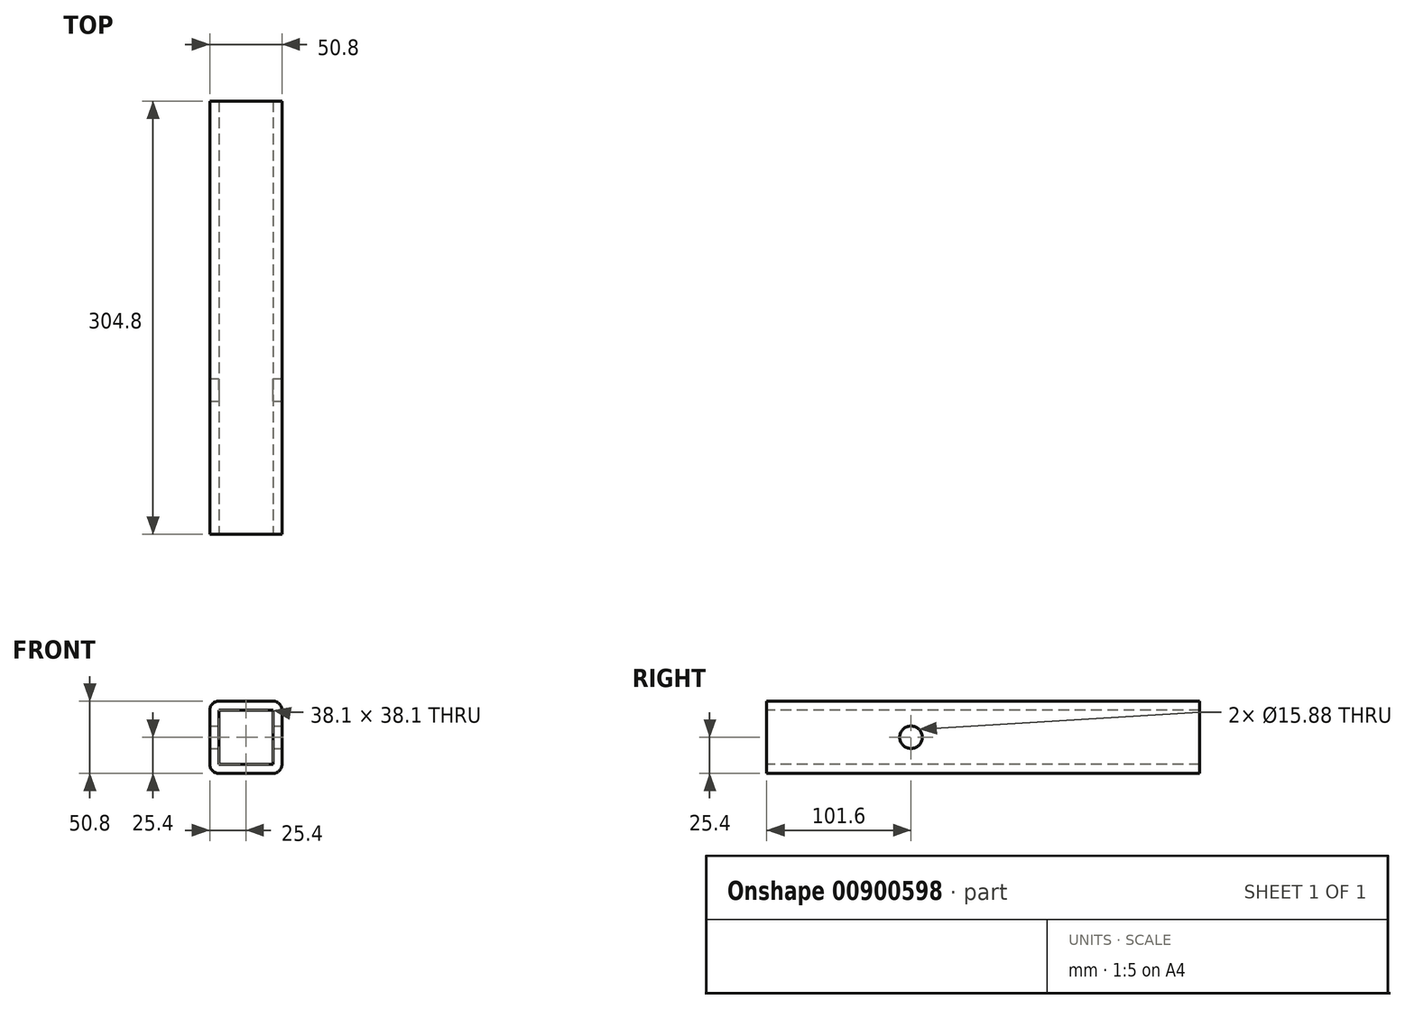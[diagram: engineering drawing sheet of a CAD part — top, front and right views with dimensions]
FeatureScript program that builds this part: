
annotation { "Feature Type Name" : "Feature", "Feature Type Description" : "" }
export const myFeature = defineFeature(function(context is Context, id is Id, definition is map)
    precondition{}
    {
        {
            var Q0;
            Q0=qCreatedBy(makeId("Front.planeOp"),FACE);
            var sketch = newSketch(context, id + "F0", { "sketchPlane" : qUnion([Q0])});
            skLineSegment(sketch, "E0", {"start": v(-6.35, 0) * mm, "end": v(-44.45, 0) * mm});
            skLineSegment(sketch, "E1", {"start": v(-50.8, 6.35) * mm, "end": v(-50.8, 44.45) * mm});
            skLineSegment(sketch, "E2", {"start": v(-44.45, 50.8) * mm, "end": v(-6.35, 50.8) * mm});
            skLineSegment(sketch, "E3", {"start": v(0, 44.45) * mm, "end": v(0, 6.35) * mm});
            skPoint(sketch, "E4.visualSharp", {"position": v(-50.8, 50.8) * mm});
            skArc(sketch, "E4.filletArc", {"start": v(-44.45, 50.8) * mm, "mid": v(-48.94, 48.94) * mm, "end": v(-50.8, 44.45) * mm});
            skPoint(sketch, "E5.visualSharp", {"position": v(0, 50.8) * mm});
            skArc(sketch, "E5.filletArc", {"start": v(0, 44.45) * mm, "mid": v(-1.86, 48.94) * mm, "end": v(-6.35, 50.8) * mm});
            skPoint(sketch, "E6.visualSharp", {"position": v(0, 0) * mm});
            skArc(sketch, "E6.filletArc", {"start": v(-6.35, 0) * mm, "mid": v(-1.86, 1.86) * mm, "end": v(0, 6.35) * mm});
            skPoint(sketch, "E7.visualSharp", {"position": v(-50.8, 0) * mm});
            skArc(sketch, "E7.filletArc", {"start": v(-50.8, 6.35) * mm, "mid": v(-48.94, 1.86) * mm, "end": v(-44.45, 0) * mm});
            skSolve(sketch);
        }
        {
            var Q0;
            Q0 = qSketchRegion(id + "F0", true);
            extrude(context, id + "F1", {"entities" : qUnion([Q0]), "depth" : 304.8 * mm, "offsetDistance" : 25.4 * mm});
        }
        {
            var Q0;
            Q0=makeQuery(id+"F1.opExtrude","CAP_FACE",FACE,{"disambiguationData":[OSD([sQuery(id+"F0.wireOp",EDGE,"E0"),sQuery(id+"F0.wireOp",EDGE,"E1"),sQuery(id+"F0.wireOp",EDGE,"E2"),sQuery(id+"F0.wireOp",EDGE,"E3"),sQuery(id+"F0.wireOp",EDGE,"E4.filletArc"),sQuery(id+"F0.wireOp",EDGE,"E5.filletArc"),sQuery(id+"F0.wireOp",EDGE,"E6.filletArc"),sQuery(id+"F0.wireOp",EDGE,"E7.filletArc")])],"isStart":false});
            var sketch = newSketch(context, id + "F2", { "sketchPlane" : qUnion([Q0])});
            skLineSegment(sketch, "E8", {"start": v(-44.45, 6.35) * mm, "end": v(-6.35, 6.35) * mm});
            skLineSegment(sketch, "E9", {"start": v(-6.35, 6.35) * mm, "end": v(-6.35, 44.45) * mm});
            skLineSegment(sketch, "E10", {"start": v(-6.35, 44.45) * mm, "end": v(-44.45, 44.45) * mm});
            skLineSegment(sketch, "E11", {"start": v(-44.45, 44.45) * mm, "end": v(-44.45, 6.35) * mm});
            skSolve(sketch);
        }
        {
            var Q0;
            Q0 = qSketchRegion(id + "F2", true);
            extrude(context, id + "F3", {"entities" : qUnion([Q0]), "operationType" : NewBodyOperationType.REMOVE, "oppositeDirection" : true, "depth" : 304.8 * mm, "offsetDistance" : 25.4 * mm});
        }
        {
            var Q0;
            Q0=makeQuery(id+"F1.opExtrude","SWEPT_FACE",FACE,{"disambiguationData":[OSD([sQuery(id+"F0.wireOp",EDGE,"E3")])]});
            var sketch = newSketch(context, id + "F4", { "sketchPlane" : qUnion([Q0])});
            skCircle(sketch, "E12", {"center": v(-203.2, 25.4) * mm, "radius": 7.94 * mm});
            skSolve(sketch);
        }
        {
            var Q0;
            Q0=makeQuery(id+"F4.imprint","IMPRINT",FACE,{"disambiguationData":[TD([[makeQuery(id+"F4.imprint","IMPRINT",EDGE,{"derivedFrom":sQuery(id+"F4.wireOp",EDGE,"E12")}),1.0]])]});
            extrude(context, id + "F5", {"entities" : qUnion([Q0]), "operationType" : NewBodyOperationType.REMOVE, "oppositeDirection" : true, "depth" : 50.8 * mm, "offsetDistance" : 25.4 * mm});
        }
    });
